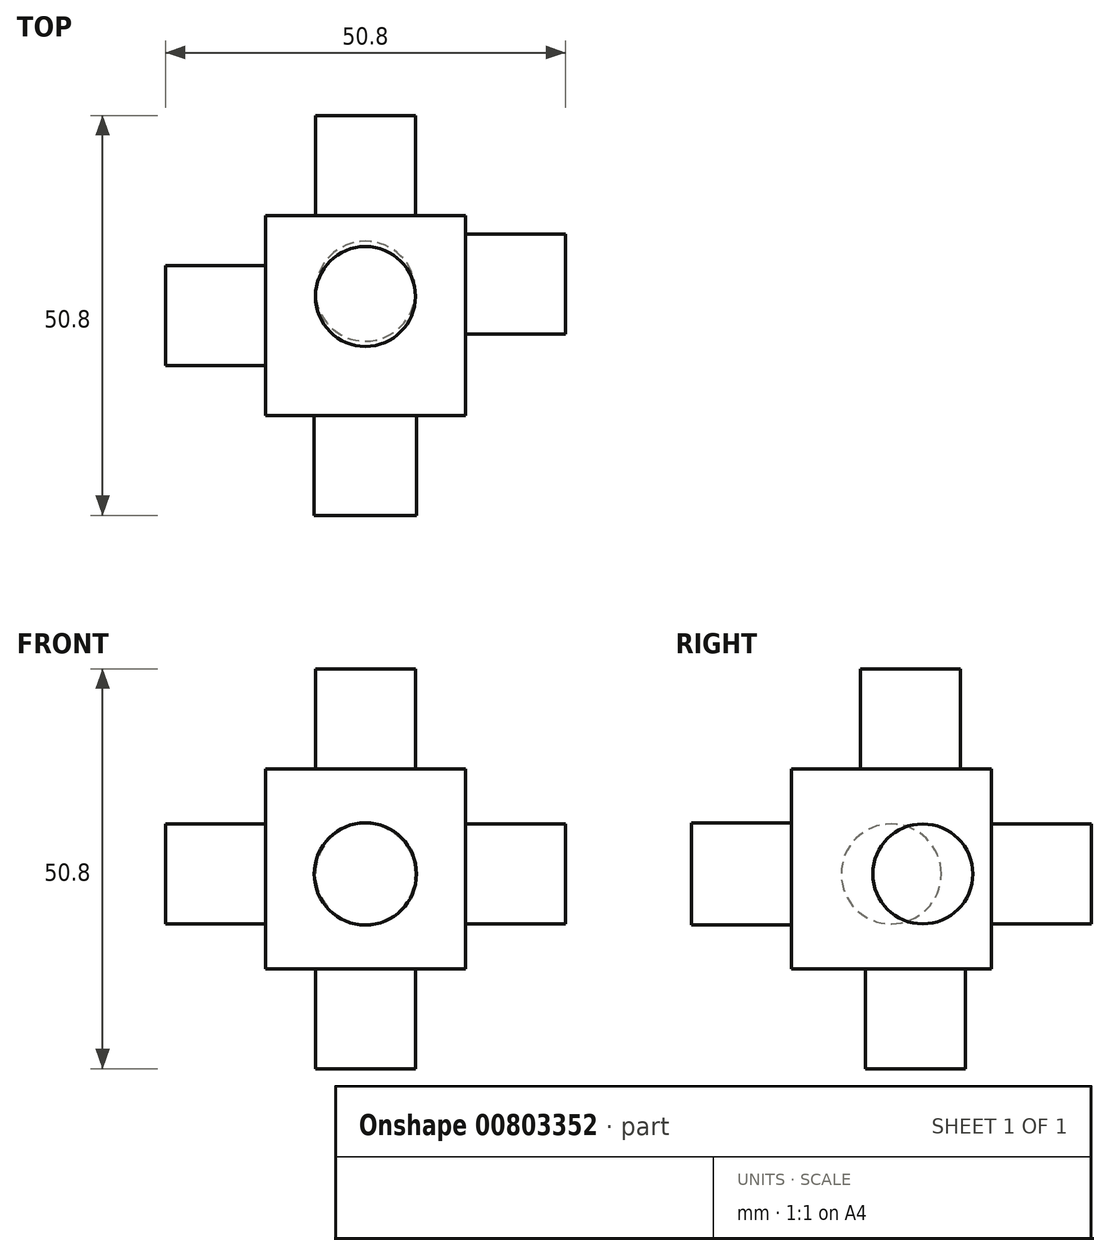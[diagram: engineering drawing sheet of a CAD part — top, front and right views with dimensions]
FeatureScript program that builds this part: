
annotation { "Feature Type Name" : "Feature", "Feature Type Description" : "" }
export const myFeature = defineFeature(function(context is Context, id is Id, definition is map)
    precondition{}
    {
        {
            var Q0;
            Q0=qCreatedBy(makeId("Front.planeOp"),FACE);
            var sketch = newSketch(context, id + "F0", { "sketchPlane" : qUnion([Q0])});
            skLineSegment(sketch, "E0", {"start": v(-12.68, 13.36) * mm, "end": v(-12.68, -12.04) * mm});
            skLineSegment(sketch, "E1", {"start": v(-12.68, -12.04) * mm, "end": v(12.72, -12.04) * mm});
            skLineSegment(sketch, "E2", {"start": v(12.72, -12.04) * mm, "end": v(12.72, 13.36) * mm});
            skLineSegment(sketch, "E3", {"start": v(12.72, 13.36) * mm, "end": v(-12.68, 13.36) * mm});
            skLineSegment(sketch, "E4", {"start": v(-12.68, 13.36) * mm, "end": v(-12.68, 11.51) * mm});
            skSolve(sketch);
        }
        {
            var Q0;
            Q0=makeQuery(id+"F0.imprint","IMPRINT",FACE,{"disambiguationData":[TD([[makeQuery(id+"F0.imprint","IMPRINT",EDGE,{"derivedFrom":sQuery(id+"F0.wireOp",EDGE,"E0")}),1.0]])]});
            extrude(context, id + "F1", {"entities" : qUnion([Q0]), "depth" : 25.4 * mm, "offsetDistance" : 25.4 * mm});
        }
        {
            var Q0;
            Q0=makeQuery(id+"F1.opExtrude","CAP_FACE",FACE,{"disambiguationData":[OSD([sQuery(id+"F0.wireOp",EDGE,"E0"),sQuery(id+"F0.wireOp",EDGE,"E1"),sQuery(id+"F0.wireOp",EDGE,"E2"),sQuery(id+"F0.wireOp",EDGE,"E3"),sQuery(id+"F0.wireOp",EDGE,"E4")])],"isStart":false});
            var sketch = newSketch(context, id + "F2", { "sketchPlane" : qUnion([Q0])});
            skCircle(sketch, "E5", {"center": v(0, 0) * mm, "radius": 6.5 * mm});
            skSolve(sketch);
        }
        {
            var Q0;
            Q0=makeQuery(id+"F1.opExtrude","CAP_FACE",FACE,{"disambiguationData":[OSD([sQuery(id+"F0.wireOp",EDGE,"E0"),sQuery(id+"F0.wireOp",EDGE,"E1"),sQuery(id+"F0.wireOp",EDGE,"E2"),sQuery(id+"F0.wireOp",EDGE,"E3"),sQuery(id+"F0.wireOp",EDGE,"E4")])],"isStart":true});
            var sketch = newSketch(context, id + "F3", { "sketchPlane" : qUnion([Q0])});
            skCircle(sketch, "E6", {"center": v(0, 0) * mm, "radius": 6.35 * mm});
            skSolve(sketch);
        }
        {
            var Q0;
            Q0=makeQuery(id+"F3.imprint","IMPRINT",FACE,{"disambiguationData":[TD([[makeQuery(id+"F3.imprint","IMPRINT",EDGE,{"derivedFrom":sQuery(id+"F3.wireOp",EDGE,"E6")}),1.0]])]});
            var Q1;
            Q1=sQuery(id+"F3.wireOp",EDGE,"E6");
            extrude(context, id + "F4", {"entities" : qUnion([Q0]), "operationType" : NewBodyOperationType.ADD, "surfaceEntities" : qUnion([Q1]), "depth" : 12.7 * mm, "offsetDistance" : 25.4 * mm});
        }
        {
            var Q0;
            Q0=makeQuery(id+"F2.imprint","IMPRINT",FACE,{"disambiguationData":[TD([[makeQuery(id+"F2.imprint","IMPRINT",EDGE,{"derivedFrom":sQuery(id+"F2.wireOp",EDGE,"E5")}),1.0]])]});
            var Q1;
            Q1=sQuery(id+"F2.wireOp",EDGE,"E5");
            extrude(context, id + "F5", {"entities" : qUnion([Q0]), "operationType" : NewBodyOperationType.ADD, "surfaceEntities" : qUnion([Q1]), "depth" : 12.7 * mm, "offsetDistance" : 25.4 * mm});
        }
        {
            var Q0;
            Q0=makeQuery(id+"F1.opExtrude","SWEPT_FACE",FACE,{"disambiguationData":[OSD([sQuery(id+"F0.wireOp",EDGE,"E3")])]});
            var sketch = newSketch(context, id + "F6", { "sketchPlane" : qUnion([Q0])});
            skCircle(sketch, "E7", {"center": v(0, -10.3) * mm, "radius": 6.35 * mm});
            skSolve(sketch);
        }
        {
            var Q0;
            Q0=makeQuery(id+"F6.imprint","IMPRINT",FACE,{"disambiguationData":[TD([[makeQuery(id+"F6.imprint","IMPRINT",EDGE,{"derivedFrom":sQuery(id+"F6.wireOp",EDGE,"E7")}),1.0]])]});
            var Q1;
            Q1=sQuery(id+"F6.wireOp",EDGE,"E7");
            extrude(context, id + "F7", {"entities" : qUnion([Q0]), "surfaceEntities" : qUnion([Q1]), "depth" : 12.7 * mm, "offsetDistance" : 25.4 * mm});
        }
        {
            var Q0;
            Q0=makeQuery(id+"F1.opExtrude","SWEPT_FACE",FACE,{"disambiguationData":[OSD([sQuery(id+"F0.wireOp",EDGE,"E0"),sQuery(id+"F0.wireOp",EDGE,"E4")])]});
            var sketch = newSketch(context, id + "F8", { "sketchPlane" : qUnion([Q0])});
            skCircle(sketch, "E8", {"center": v(12.73, 0) * mm, "radius": 6.35 * mm});
            skSolve(sketch);
        }
        {
            var Q0;
            Q0=makeQuery(id+"F8.imprint","IMPRINT",FACE,{"disambiguationData":[TD([[makeQuery(id+"F8.imprint","IMPRINT",EDGE,{"derivedFrom":sQuery(id+"F8.wireOp",EDGE,"E8")}),1.0]])]});
            extrude(context, id + "F9", {"entities" : qUnion([Q0]), "depth" : 12.7 * mm, "offsetDistance" : 25.4 * mm});
        }
        {
            var Q0;
            Q0=makeQuery(id+"F1.opExtrude","SWEPT_FACE",FACE,{"disambiguationData":[OSD([sQuery(id+"F0.wireOp",EDGE,"E1")])]});
            var sketch = newSketch(context, id + "F10", { "sketchPlane" : qUnion([Q0])});
            skCircle(sketch, "E9", {"center": v(0, 9.64) * mm, "radius": 6.35 * mm});
            skSolve(sketch);
        }
        {
            var Q0;
            Q0=makeQuery(id+"F10.imprint","IMPRINT",FACE,{"disambiguationData":[TD([[makeQuery(id+"F10.imprint","IMPRINT",EDGE,{"derivedFrom":sQuery(id+"F10.wireOp",EDGE,"E9")}),1.0]])]});
            var Q1;
            Q1=sQuery(id+"F10.wireOp",EDGE,"E9");
            extrude(context, id + "F11", {"entities" : qUnion([Q0]), "surfaceEntities" : qUnion([Q1]), "depth" : 12.7 * mm, "offsetDistance" : 25.4 * mm});
        }
        {
            var Q0;
            Q0=makeQuery(id+"F1.opExtrude","SWEPT_FACE",FACE,{"disambiguationData":[OSD([sQuery(id+"F0.wireOp",EDGE,"E2")])]});
            var sketch = newSketch(context, id + "F12", { "sketchPlane" : qUnion([Q0])});
            skCircle(sketch, "E10", {"center": v(-8.72, 0) * mm, "radius": 6.35 * mm});
            skSolve(sketch);
        }
        {
            var Q0;
            Q0=makeQuery(id+"F12.imprint","IMPRINT",FACE,{"disambiguationData":[TD([[makeQuery(id+"F12.imprint","IMPRINT",EDGE,{"derivedFrom":sQuery(id+"F12.wireOp",EDGE,"E10")}),1.0]])]});
            extrude(context, id + "F13", {"entities" : qUnion([Q0]), "depth" : 12.7 * mm, "offsetDistance" : 25.4 * mm});
        }
    });
